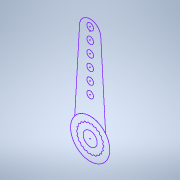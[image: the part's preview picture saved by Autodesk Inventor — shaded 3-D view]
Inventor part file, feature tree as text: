
AUTODESK INVENTOR PART (.ipt)
format: ipt  version: 2021.1 (Build 251245010, 245A)  size: 99,840 bytes
history: native  units: mm
features: sketch x1
ambient origin geometry x8: Origin, YZ Plane, XZ Plane, XY Plane, X Axis, Y Axis, Z Axis, Center Point
feature tree (1):
  sketch  "Sketch1"
